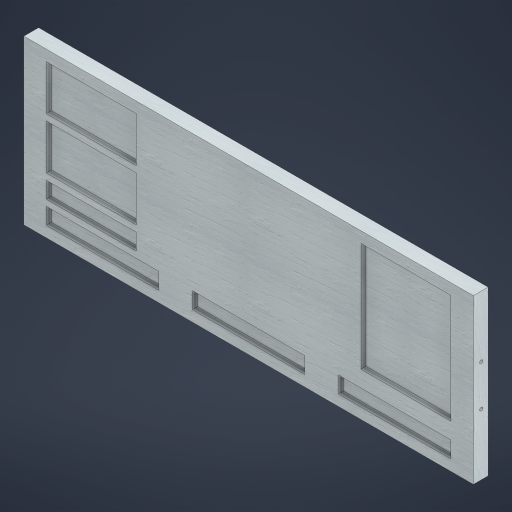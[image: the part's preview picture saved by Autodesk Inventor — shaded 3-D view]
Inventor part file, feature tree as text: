
AUTODESK INVENTOR PART (.ipt)
format: ipt  version: 2024 (Build 280153000, 153)  size: 436,736 bytes
history: native  units: mm
features: extrude x4, sketch x2, other x1
ambient origin geometry x8: Origin, YZ Plane, XZ Plane, XY Plane, X Axis, Y Axis, Z Axis, Center Point
bodies: Body1 (feature_tree)
feature tree (7):
  other  "Sólido1"
  extrude  "Extrusión1"  Depth=137.5mm
  extrude  "Extrusión2"  Depth=27.5mm
  extrude  "Extrusión3"  Depth=137.5mm
  extrude  "Extrusión4"  Depth=20.0mm
  sketch  "Boceto2"  dims[d3=0.0mm d4=137.5mm]
  sketch  "Boceto4"  dims[d5=20.0mm d6=27.5mm d7=137.5mm d8=20.0mm d9=27.5mm d10=13.333333mm d11=13.333333mm d12=137.5mm d13=41.25mm d14=41.25mm d15=20.0mm d17=110.0mm d18=133.333333mm d19=27.5mm d20=13.333333mm d21=110.0mm d22=55.0mm d23=27.5mm d24=13.333333mm d25=110.0mm d26=55.0mm d27=27.5mm d28=7.843137mm d29=110.0mm d30=20.0mm d31=7.843137mm d32=7.647059mm d33=6.0mm d34=0.0mm d35=9.0mm d36=9.0mm d37=9.0mm d38=9.0mm d39=9.0mm d40=66.666667mm d41=9.0mm d42=66.666667mm d43=9.0mm d44=66.666667mm d45=9.0mm d46=66.666667mm d47=6.0mm d48=0.0mm d49=4.0mm d50=4.0mm d51=50.0mm d52=75.0mm d53=600.0mm d54=0.0mm]
